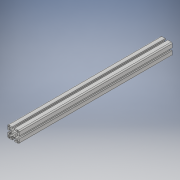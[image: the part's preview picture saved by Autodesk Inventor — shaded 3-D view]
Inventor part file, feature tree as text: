
AUTODESK INVENTOR PART (.ipt)
format: ipt  version: 2019 (Build 230136000, 136)  size: 196,608 bytes
history: native  units: in
note: dims shown in document units (in); Inventor stores cm internally (conversion verified against a paired STEP export)
features: extrude x1, sketch x1, other x1
ambient origin geometry x8: Origin, YZ Plane, XZ Plane, XY Plane, X Axis, Y Axis, Z Axis, Center Point
bodies: Solid1 (feature_tree)
feature tree (3):
  extrude  "Extrusion1"  [1 undecoded]
  sketch  "Sketch1"  dims[d0=20.0in d1=0.0in]
  other  "Boss-Extrude1"
note: 1 required parameter value undecoded (feature->parameter linkage not recoverable at this tier; creation-order binding heuristic only, values carry confidence <= 0.55)
